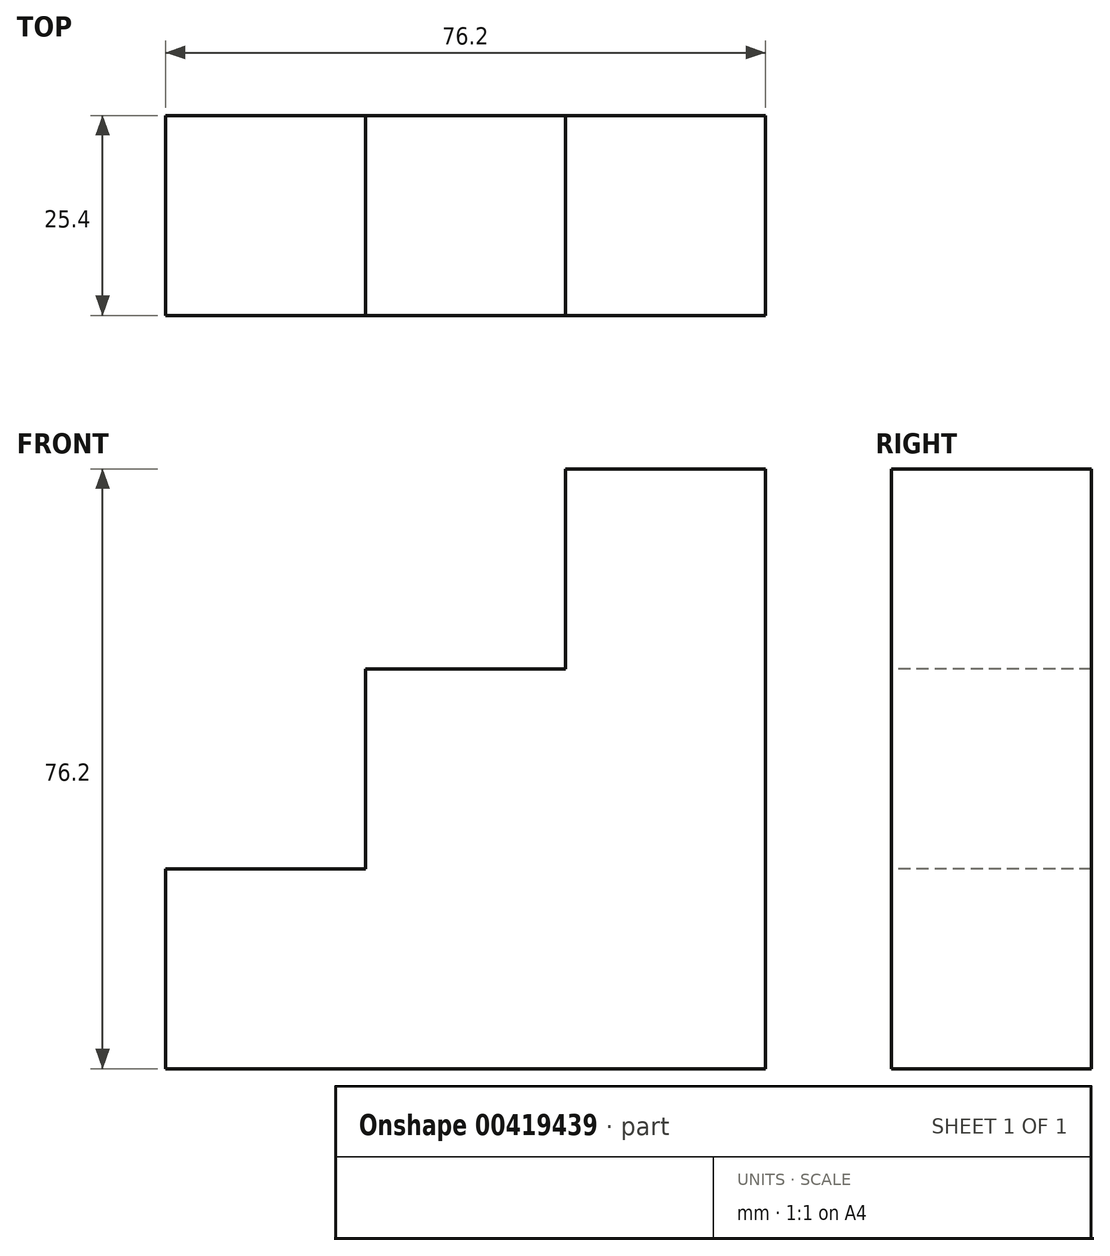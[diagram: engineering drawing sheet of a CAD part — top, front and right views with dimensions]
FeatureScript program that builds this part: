
annotation { "Feature Type Name" : "Feature", "Feature Type Description" : "" }
export const myFeature = defineFeature(function(context is Context, id is Id, definition is map)
    precondition{}
    {
        {
            var Q0;
            Q0=qCreatedBy(makeId("Front.planeOp"),FACE);
            var sketch = newSketch(context, id + "F0", { "sketchPlane" : qUnion([Q0])});
            skLineSegment(sketch, "E0", {"start": v(-76.2, -25.63) * mm, "end": v(0, -25.63) * mm});
            skLineSegment(sketch, "E1", {"start": v(0, -25.63) * mm, "end": v(0, 50.57) * mm});
            skLineSegment(sketch, "E2", {"start": v(0, 50.57) * mm, "end": v(-25.4, 50.57) * mm});
            skLineSegment(sketch, "E3", {"start": v(-25.4, 50.57) * mm, "end": v(-25.4, 25.17) * mm});
            skLineSegment(sketch, "E4", {"start": v(-25.4, 25.17) * mm, "end": v(-50.8, 25.17) * mm});
            skLineSegment(sketch, "E5", {"start": v(-50.8, 25.17) * mm, "end": v(-50.8, -0.23) * mm});
            skLineSegment(sketch, "E6", {"start": v(-50.8, -0.23) * mm, "end": v(-76.2, -0.23) * mm});
            skLineSegment(sketch, "E7", {"start": v(-76.2, -0.23) * mm, "end": v(-76.2, -25.63) * mm});
            skSolve(sketch);
        }
        {
            var Q0;
            Q0 = qSketchRegion(id + "F0", true);
            extrude(context, id + "F1", {"entities" : qUnion([Q0]), "oppositeDirection" : true, "depth" : 25.4 * mm});
        }
    });
